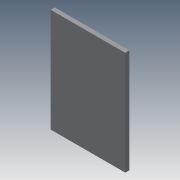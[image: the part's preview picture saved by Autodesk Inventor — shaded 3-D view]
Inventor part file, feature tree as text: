
AUTODESK INVENTOR PART (.ipt)
format: ipt  version: 2015 (Build 190159000, 159)  size: 94,720 bytes
history: native  units: mm
features: other x5, extrude x1, sketch x1, projected_geometry x1
ambient origin geometry x8: Origin, YZ Plane, XZ Plane, XY Plane, X Axis, Y Axis, Z Axis, Center Point
bodies: Body1 (feature_tree)
feature tree (8):
  other  "Blocks"
  extrude  "Extrusion2"  Depth=180.0mm
  sketch  "Sketch2"  dims[d1=250.0mm d2=180.0mm d5=5.0mm d6=10.0mm d7=20.0mm d8=90.0mm d9=125.0mm d10=10.0mm d11=0.0mm]
  other  "DXF"
  projected_geometry  "Projected Loop1"
  other  "Block1"
  other  "Block1:1"
  other  "Block1:2"
